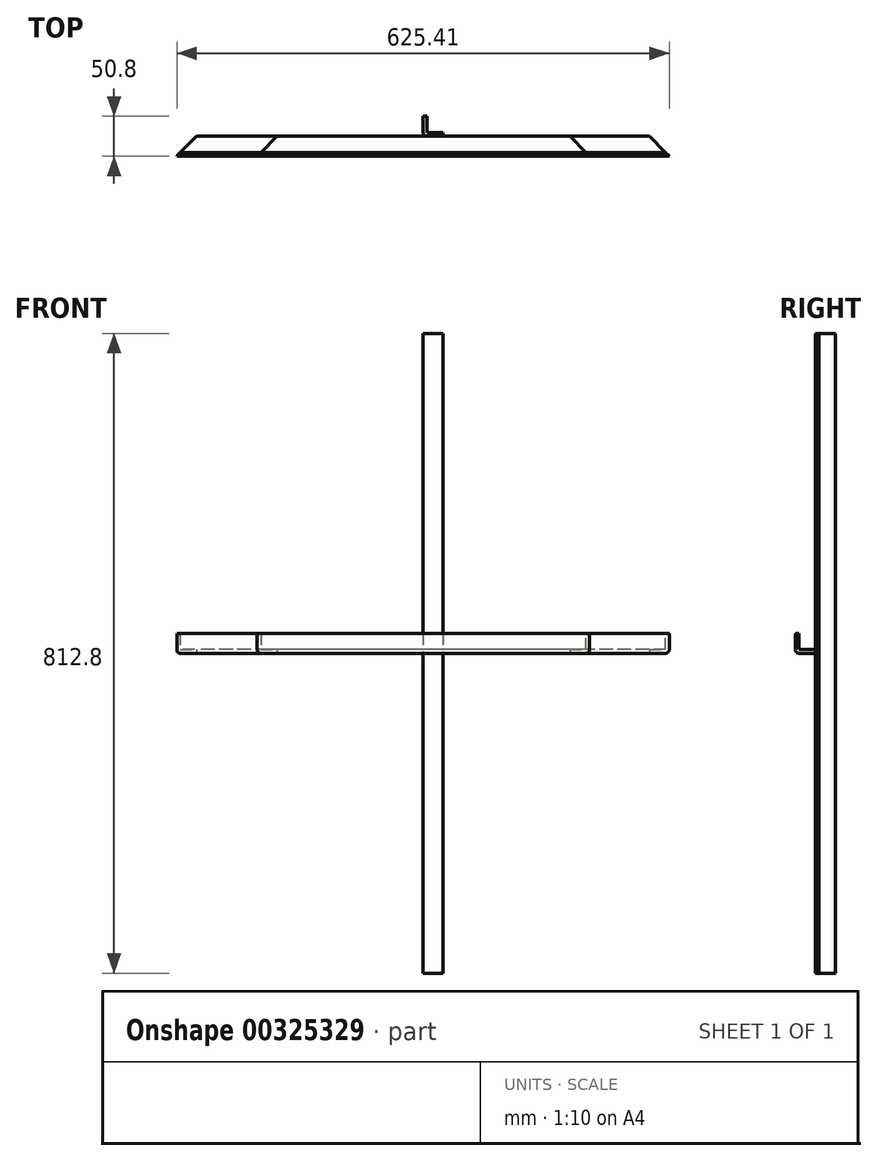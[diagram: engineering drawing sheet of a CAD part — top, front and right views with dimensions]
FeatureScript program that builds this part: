
annotation { "Feature Type Name" : "Feature", "Feature Type Description" : "" }
export const myFeature = defineFeature(function(context is Context, id is Id, definition is map)
    precondition{}
    {
        {
            var Q0;
            Q0=qCreatedBy(makeId("Right.planeOp"),FACE);
            var sketch = newSketch(context, id + "F0", { "sketchPlane" : qUnion([Q0])});
            skLineSegment(sketch, "E0", {"start": v(0, 0) * mm, "end": v(0, 4.76) * mm});
            skLineSegment(sketch, "E1", {"start": v(0, 4.76) * mm, "end": v(-20.64, 4.76) * mm});
            skLineSegment(sketch, "E2", {"start": v(-20.64, 4.76) * mm, "end": v(-20.64, 25.4) * mm});
            skLineSegment(sketch, "E3", {"start": v(-20.64, 25.4) * mm, "end": v(-25.4, 25.4) * mm});
            skLineSegment(sketch, "E4", {"start": v(-25.4, 25.4) * mm, "end": v(-25.4, 0) * mm});
            skLineSegment(sketch, "E5", {"start": v(-25.4, 0) * mm, "end": v(0, 0) * mm});
            skSolve(sketch);
        }
        {
            var Q0;
            Q0=makeQuery(id+"F0.imprint","IMPRINT",FACE,{"disambiguationData":[TD([[makeQuery(id+"F0.imprint","IMPRINT",EDGE,{"derivedFrom":sQuery(id+"F0.wireOp",EDGE,"E0")}),1.0]])]});
            extrude(context, id + "F1", {"entities" : qUnion([Q0]), "endBound" : BoundingType.SYMMETRIC, "depth" : 625.47 * mm});
        }
        {
            var Q0;
            Q0=makeQuery(id+"F1.opExtrude","SWEPT_EDGE",EDGE,{"disambiguationData":[OSD([sQuery(id+"F0.wireOp",EDGE,"E4"),sQuery(id+"F0.wireOp",EDGE,"E5")])]});
            fillet(context, id + "F2", {"entities" : qUnion([Q0]), "radius" : 5.08 * mm, "tangentPropagation" : true, "allowEdgeOverflow" : false});
        }
        {
            var Q0;
            Q0=qCreatedBy(makeId("Top.planeOp"),FACE);
            var sketch = newSketch(context, id + "F3", { "sketchPlane" : qUnion([Q0])});
            skLineSegment(sketch, "E6", {"start": v(0, 0) * mm, "end": v(0, -152.4) * mm});
            skLineSegment(sketch, "E7", {"start": v(0, -152.4) * mm, "end": v(-152.4, -152.4) * mm});
            skLineSegment(sketch, "E8", {"start": v(-152.4, -152.4) * mm, "end": v(0, 0) * mm});
            skLineSegment(sketch, "E9", {"start": v(-152.4, -152.4) * mm, "end": v(-152.4, 0) * mm});
            skLineSegment(sketch, "E10", {"start": v(-152.4, 0) * mm, "end": v(0, 0) * mm});
            skLineSegment(sketch, "E11", {"start": v(0, 0) * mm, "end": v(0, 25.4) * mm});
            skLineSegment(sketch, "E12", {"start": v(0, 25.4) * mm, "end": v(4.76, 25.4) * mm});
            skLineSegment(sketch, "E13", {"start": v(4.76, 25.4) * mm, "end": v(4.76, 4.76) * mm});
            skLineSegment(sketch, "E14", {"start": v(4.76, 4.76) * mm, "end": v(25.4, 4.76) * mm});
            skLineSegment(sketch, "E15", {"start": v(25.4, 4.76) * mm, "end": v(25.4, 0) * mm});
            skLineSegment(sketch, "E16", {"start": v(25.4, 0) * mm, "end": v(0, 0) * mm});
            skSolve(sketch);
        }
        {
            var Q0;
            Q0=makeQuery(id+"F3.imprint","IMPRINT",FACE,{"disambiguationData":[TD([[makeQuery(id+"F3.imprint","IMPRINT",EDGE,{"derivedFrom":sQuery(id+"F3.wireOp",EDGE,"E8")}),1.0]])]});
            extrude(context, id + "F4", {"entities" : qUnion([Q0]), "depth" : 152.4 * mm});
        }
        {
            var Q0;
            Q0=makeQuery(id+"F4.opExtrude","SWEPT_BODY",BODY,{"disambiguationData":[OSD([sQuery(id+"F3.wireOp",EDGE,"E8"),sQuery(id+"F3.wireOp",EDGE,"E9"),sQuery(id+"F3.wireOp",EDGE,"E10")])]});
            transform(context, id + "F5", {"entities" : qUnion([Q0]), "transformType" : TransformType.TRANSLATION_3D, "dx" : -287.97 * mm, "dy" : 0 * mm, "dz" : 0 * mm, "makeCopy" : false});
        }
        {
            var Q0;
            Q0=makeQuery(id+"F4.opExtrude","SWEPT_BODY",BODY,{"disambiguationData":[OSD([sQuery(id+"F3.wireOp",EDGE,"E8"),sQuery(id+"F3.wireOp",EDGE,"E9"),sQuery(id+"F3.wireOp",EDGE,"E10")])]});
            var Q1;
            Q1=makeQuery(id+"F1.opExtrude","SWEPT_BODY",BODY,{"disambiguationData":[OSD([sQuery(id+"F0.wireOp",EDGE,"E0"),sQuery(id+"F0.wireOp",EDGE,"E1"),sQuery(id+"F0.wireOp",EDGE,"E2"),sQuery(id+"F0.wireOp",EDGE,"E3"),sQuery(id+"F0.wireOp",EDGE,"E4"),sQuery(id+"F0.wireOp",EDGE,"E5")])]});
            booleanBodies(context, id + "F6", {"operationType" : BooleanOperationType.SUBTRACTION, "tools" : qUnion([Q0]), "targets" : qUnion([Q1])});
        }
        {
            var Q0;
            Q0=makeQuery(id+"F3.imprint","IMPRINT",FACE,{"disambiguationData":[TD([[makeQuery(id+"F3.imprint","IMPRINT",EDGE,{"derivedFrom":sQuery(id+"F3.wireOp",EDGE,"E8")}),1.0]])]});
            extrude(context, id + "F7", {"entities" : qUnion([Q0]), "depth" : 152.4 * mm});
        }
        {
            var Q0;
            Q0=makeQuery(id+"F7.opExtrude","SWEPT_BODY",BODY,{"disambiguationData":[OSD([sQuery(id+"F3.wireOp",EDGE,"E8"),sQuery(id+"F3.wireOp",EDGE,"E9"),sQuery(id+"F3.wireOp",EDGE,"E10")])]});
            var Q1;
            Q1=makeQuery(id+"F7.opExtrude","SWEPT_EDGE",EDGE,{"disambiguationData":[OSD([sQuery(id+"F3.wireOp",EDGE,"E9"),sQuery(id+"F3.wireOp",EDGE,"E10")])]});
            transform(context, id + "F8", {"entities" : qUnion([Q0]), "transformType" : TransformType.ROTATION, "transformAxis" : qUnion([Q1]), "angle" : 90 * degree, "makeCopy" : false});
        }
        {
            var Q0;
            Q0=makeQuery(id+"F7.opExtrude","SWEPT_BODY",BODY,{"disambiguationData":[OSD([sQuery(id+"F3.wireOp",EDGE,"E8"),sQuery(id+"F3.wireOp",EDGE,"E9"),sQuery(id+"F3.wireOp",EDGE,"E10")])]});
            transform(context, id + "F9", {"entities" : qUnion([Q0]), "transformType" : TransformType.TRANSLATION_3D, "dx" : 592.07 * mm, "dy" : 0 * mm, "dz" : 0 * mm, "makeCopy" : false});
        }
        {
            var Q0;
            Q0=makeQuery(id+"F7.opExtrude","SWEPT_BODY",BODY,{"disambiguationData":[OSD([sQuery(id+"F3.wireOp",EDGE,"E8"),sQuery(id+"F3.wireOp",EDGE,"E9"),sQuery(id+"F3.wireOp",EDGE,"E10")])]});
            var Q1;
            Q1=makeQuery(id+"F1.opExtrude","SWEPT_BODY",BODY,{"disambiguationData":[OSD([sQuery(id+"F0.wireOp",EDGE,"E0"),sQuery(id+"F0.wireOp",EDGE,"E1"),sQuery(id+"F0.wireOp",EDGE,"E2"),sQuery(id+"F0.wireOp",EDGE,"E3"),sQuery(id+"F0.wireOp",EDGE,"E4"),sQuery(id+"F0.wireOp",EDGE,"E5")])]});
            booleanBodies(context, id + "F10", {"operationType" : BooleanOperationType.SUBTRACTION, "tools" : qUnion([Q0]), "targets" : qUnion([Q1])});
        }
        {
            var Q0;
            Q0=makeQuery(id+"F0.imprint","IMPRINT",FACE,{"disambiguationData":[TD([[makeQuery(id+"F0.imprint","IMPRINT",EDGE,{"derivedFrom":sQuery(id+"F0.wireOp",EDGE,"E0")}),1.0]])]});
            extrude(context, id + "F11", {"entities" : qUnion([Q0]), "endBound" : BoundingType.SYMMETRIC, "depth" : 422.27 * mm});
        }
        {
            var Q0;
            Q0=makeQuery(id+"F11.opExtrude","SWEPT_EDGE",EDGE,{"disambiguationData":[OSD([sQuery(id+"F0.wireOp",EDGE,"E4"),sQuery(id+"F0.wireOp",EDGE,"E5")])]});
            fillet(context, id + "F12", {"entities" : qUnion([Q0]), "radius" : 5.08 * mm, "tangentPropagation" : true, "allowEdgeOverflow" : false});
        }
        {
            var Q0;
            Q0=makeQuery(id+"F3.imprint","IMPRINT",FACE,{"disambiguationData":[TD([[makeQuery(id+"F3.imprint","IMPRINT",EDGE,{"derivedFrom":sQuery(id+"F3.wireOp",EDGE,"E8")}),1.0]])]});
            extrude(context, id + "F13", {"entities" : qUnion([Q0]), "depth" : 152.4 * mm});
        }
        {
            var Q0;
            Q0=makeQuery(id+"F13.opExtrude","SWEPT_BODY",BODY,{"disambiguationData":[OSD([sQuery(id+"F3.wireOp",EDGE,"E8"),sQuery(id+"F3.wireOp",EDGE,"E9"),sQuery(id+"F3.wireOp",EDGE,"E10")])]});
            transform(context, id + "F14", {"entities" : qUnion([Q0]), "transformType" : TransformType.TRANSLATION_3D, "dx" : -185.42 * mm, "dy" : 0 * mm, "dz" : 0 * mm, "makeCopy" : false});
        }
        {
            var Q0;
            Q0=makeQuery(id+"F13.opExtrude","SWEPT_BODY",BODY,{"disambiguationData":[OSD([sQuery(id+"F3.wireOp",EDGE,"E8"),sQuery(id+"F3.wireOp",EDGE,"E9"),sQuery(id+"F3.wireOp",EDGE,"E10")])]});
            var Q1;
            Q1=makeQuery(id+"F11.opExtrude","SWEPT_BODY",BODY,{"disambiguationData":[OSD([sQuery(id+"F0.wireOp",EDGE,"E0"),sQuery(id+"F0.wireOp",EDGE,"E1"),sQuery(id+"F0.wireOp",EDGE,"E2"),sQuery(id+"F0.wireOp",EDGE,"E3"),sQuery(id+"F0.wireOp",EDGE,"E4"),sQuery(id+"F0.wireOp",EDGE,"E5")])]});
            booleanBodies(context, id + "F15", {"operationType" : BooleanOperationType.SUBTRACTION, "tools" : qUnion([Q0]), "targets" : qUnion([Q1])});
        }
        {
            var Q0;
            Q0=makeQuery(id+"F3.imprint","IMPRINT",FACE,{"disambiguationData":[TD([[makeQuery(id+"F3.imprint","IMPRINT",EDGE,{"derivedFrom":sQuery(id+"F3.wireOp",EDGE,"E8")}),1.0]])]});
            extrude(context, id + "F16", {"entities" : qUnion([Q0]), "depth" : 152.4 * mm});
        }
        {
            var Q0;
            Q0=makeQuery(id+"F16.opExtrude","SWEPT_BODY",BODY,{"disambiguationData":[OSD([sQuery(id+"F3.wireOp",EDGE,"E8"),sQuery(id+"F3.wireOp",EDGE,"E9"),sQuery(id+"F3.wireOp",EDGE,"E10")])]});
            var Q1;
            Q1=makeQuery(id+"F16.opExtrude","SWEPT_EDGE",EDGE,{"disambiguationData":[OSD([sQuery(id+"F3.wireOp",EDGE,"E9"),sQuery(id+"F3.wireOp",EDGE,"E10")])]});
            transform(context, id + "F17", {"entities" : qUnion([Q0]), "transformType" : TransformType.ROTATION, "transformAxis" : qUnion([Q1]), "angle" : 90 * degree, "makeCopy" : false});
        }
        {
            var Q0;
            Q0=makeQuery(id+"F16.opExtrude","SWEPT_BODY",BODY,{"disambiguationData":[OSD([sQuery(id+"F3.wireOp",EDGE,"E8"),sQuery(id+"F3.wireOp",EDGE,"E9"),sQuery(id+"F3.wireOp",EDGE,"E10")])]});
            transform(context, id + "F18", {"entities" : qUnion([Q0]), "transformType" : TransformType.TRANSLATION_3D, "dx" : 490.98 * mm, "dy" : 0 * mm, "dz" : 0 * mm, "makeCopy" : false});
        }
        {
            var Q0;
            Q0=makeQuery(id+"F16.opExtrude","SWEPT_BODY",BODY,{"disambiguationData":[OSD([sQuery(id+"F3.wireOp",EDGE,"E8"),sQuery(id+"F3.wireOp",EDGE,"E9"),sQuery(id+"F3.wireOp",EDGE,"E10")])]});
            var Q1;
            Q1=makeQuery(id+"F11.opExtrude","SWEPT_BODY",BODY,{"disambiguationData":[OSD([sQuery(id+"F0.wireOp",EDGE,"E0"),sQuery(id+"F0.wireOp",EDGE,"E1"),sQuery(id+"F0.wireOp",EDGE,"E2"),sQuery(id+"F0.wireOp",EDGE,"E3"),sQuery(id+"F0.wireOp",EDGE,"E4"),sQuery(id+"F0.wireOp",EDGE,"E5")])]});
            booleanBodies(context, id + "F19", {"operationType" : BooleanOperationType.SUBTRACTION, "tools" : qUnion([Q0]), "targets" : qUnion([Q1])});
        }
        {
            var Q0;
            Q0=makeQuery(id+"F3.imprint","IMPRINT",FACE,{"disambiguationData":[TD([[makeQuery(id+"F3.imprint","IMPRINT",EDGE,{"derivedFrom":sQuery(id+"F3.wireOp",EDGE,"E11")}),-1.0]])]});
            extrude(context, id + "F20", {"entities" : qUnion([Q0]), "endBound" : BoundingType.SYMMETRIC, "depth" : 812.8 * mm});
        }
        {
            var Q0;
            Q0=makeQuery(id+"F20.opExtrude","SWEPT_EDGE",EDGE,{"disambiguationData":[OSD([sQuery(id+"F3.wireOp",EDGE,"E6"),sQuery(id+"F3.wireOp",EDGE,"E8"),sQuery(id+"F3.wireOp",EDGE,"E10"),sQuery(id+"F3.wireOp",EDGE,"E11"),sQuery(id+"F3.wireOp",EDGE,"E16")])]});
            fillet(context, id + "F21", {"entities" : qUnion([Q0]), "radius" : 5.08 * mm, "tangentPropagation" : true, "allowEdgeOverflow" : false});
        }
    });
